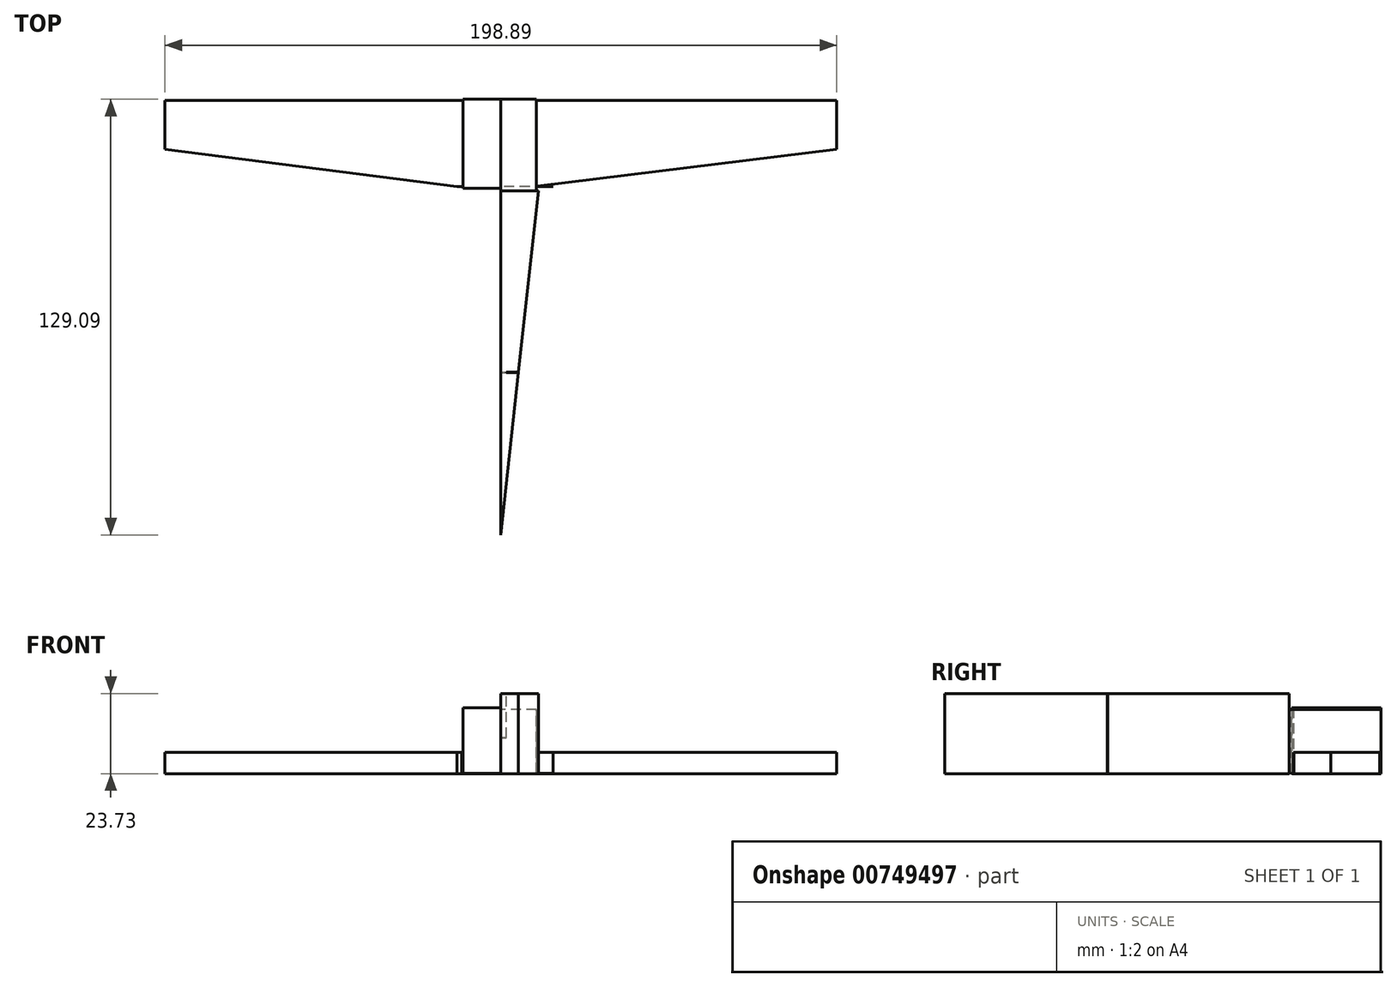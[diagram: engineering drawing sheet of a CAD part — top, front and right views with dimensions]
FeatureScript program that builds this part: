
annotation { "Feature Type Name" : "Feature", "Feature Type Description" : "" }
export const myFeature = defineFeature(function(context is Context, id is Id, definition is map)
    precondition{}
    {
        {
            var Q0;
            Q0=qCreatedBy(makeId("Top.planeOp"),FACE);
            var sketch = newSketch(context, id + "F0", { "sketchPlane" : qUnion([Q0])});
            skLineSegment(sketch, "E0.bottom", {"start": v(99.53, 14.5) * mm, "end": v(-99.36, 14.5) * mm});
            skLineSegment(sketch, "E0.top", {"start": v(99.53, -11.1) * mm, "end": v(-99.36, -11.1) * mm});
            skLineSegment(sketch, "E0.left", {"start": v(99.53, 14.5) * mm, "end": v(99.53, -11.1) * mm});
            skLineSegment(sketch, "E0.right", {"start": v(-99.36, 14.5) * mm, "end": v(-99.36, -11.1) * mm});
            skSolve(sketch);
        }
        {
            var Q0;
            Q0 = qSketchRegion(id + "F0", true);
            extrude(context, id + "F1", {"entities" : qUnion([Q0]), "depth" : 6.35 * mm, "offsetDistance" : 25.4 * mm});
        }
        {
            var Q0;
            Q0=qCreatedBy(makeId("Top.planeOp"),FACE);
            var sketch = newSketch(context, id + "F2", { "sketchPlane" : qUnion([Q0])});
            skLineSegment(sketch, "E1.bottom", {"start": v(-11.18, 14.82) * mm, "end": v(10.66, 14.82) * mm});
            skLineSegment(sketch, "E1.top", {"start": v(-11.18, -76.16) * mm, "end": v(10.66, -76.16) * mm});
            skLineSegment(sketch, "E1.left", {"start": v(-11.18, 14.82) * mm, "end": v(-11.18, -76.16) * mm});
            skLineSegment(sketch, "E1.right", {"start": v(10.66, 14.82) * mm, "end": v(10.66, -76.16) * mm});
            skSolve(sketch);
        }
        {
            var Q0;
            Q0 = qSketchRegion(id + "F2", true);
            extrude(context, id + "F3", {"entities" : qUnion([Q0]), "operationType" : NewBodyOperationType.ADD, "depth" : 25.4 * mm, "offsetDistance" : 25.4 * mm});
        }
        {
            var Q0;
            Q0=qCreatedBy(makeId("Right.planeOp"),FACE);
            var sketch = newSketch(context, id + "F4", { "sketchPlane" : qUnion([Q0])});
            skLineSegment(sketch, "E2", {"start": v(-11.26, 0) * mm, "end": v(-76.37, 12.55) * mm});
            skLineSegment(sketch, "E3", {"start": v(-76.37, 12.55) * mm, "end": v(-76.37, 0) * mm});
            skLineSegment(sketch, "E4", {"start": v(-76.37, 0) * mm, "end": v(-11.26, 0) * mm});
            skSolve(sketch);
        }
        {
            var Q0;
            Q0 = qSketchRegion(id + "F4", true);
            extrude(context, id + "F5", {"entities" : qUnion([Q0]), "operationType" : NewBodyOperationType.REMOVE, "oppositeDirection" : true, "depth" : 14.73 * mm, "offsetDistance" : 25.4 * mm});
        }
        {
            var Q0;
            Q0=qCreatedBy(makeId("Right.planeOp"),FACE);
            var sketch = newSketch(context, id + "F6", { "sketchPlane" : qUnion([Q0])});
            skLineSegment(sketch, "E5", {"start": v(-11.02, 0) * mm, "end": v(-75.8, 12.55) * mm});
            skLineSegment(sketch, "E6", {"start": v(-75.8, 12.55) * mm, "end": v(-75.8, 0) * mm});
            skLineSegment(sketch, "E7", {"start": v(-75.8, 0) * mm, "end": v(-11.02, 0) * mm});
            skSolve(sketch);
        }
        {
            var Q0;
            Q0 = qSketchRegion(id + "F6", true);
            extrude(context, id + "F7", {"entities" : qUnion([Q0]), "operationType" : NewBodyOperationType.REMOVE, "depth" : 19.56 * mm, "offsetDistance" : 25.4 * mm});
        }
        {
            var Q0;
            Q0=qCreatedBy(makeId("Right.planeOp"),FACE);
            var sketch = newSketch(context, id + "F8", { "sketchPlane" : qUnion([Q0])});
            skLineSegment(sketch, "E8", {"start": v(-74.42, 11.26) * mm, "end": v(-78.63, 14.66) * mm});
            skLineSegment(sketch, "E9", {"start": v(-78.63, 14.66) * mm, "end": v(-78.63, -1.38) * mm});
            skLineSegment(sketch, "E10", {"start": v(-78.63, -1.38) * mm, "end": v(-71.83, -1.38) * mm});
            skLineSegment(sketch, "E11", {"start": v(-71.83, -1.38) * mm, "end": v(-74.42, 9.96) * mm});
            skLineSegment(sketch, "E12", {"start": v(-74.42, 9.96) * mm, "end": v(-74.42, 11.26) * mm});
            skSolve(sketch);
        }
        {
            var Q0;
            Q0 = qSketchRegion(id + "F8", true);
            extrude(context, id + "F9", {"entities" : qUnion([Q0]), "operationType" : NewBodyOperationType.REMOVE, "depth" : 22.1 * mm, "offsetDistance" : 25.4 * mm});
        }
        {
            var Q0;
            Q0=qCreatedBy(makeId("Top.planeOp"),FACE);
            var sketch = newSketch(context, id + "F10", { "sketchPlane" : qUnion([Q0])});
            skLineSegment(sketch, "E13", {"start": v(-11.18, -11.1) * mm, "end": v(0, -76.2) * mm});
            skLineSegment(sketch, "E14", {"start": v(0, -76.2) * mm, "end": v(-11.01, -76.2) * mm});
            skLineSegment(sketch, "E15", {"start": v(-11.01, -76.2) * mm, "end": v(-11.18, -11.1) * mm});
            skSolve(sketch);
        }
        {
            var Q0;
            Q0 = qSketchRegion(id + "F10", true);
            extrude(context, id + "F11", {"entities" : qUnion([Q0]), "operationType" : NewBodyOperationType.REMOVE, "depth" : 46.48 * mm, "offsetDistance" : 25.4 * mm});
        }
        {
            var Q0;
            Q0=qCreatedBy(makeId("Top.planeOp"),FACE);
            var sketch = newSketch(context, id + "F12", { "sketchPlane" : qUnion([Q0])});
            skLineSegment(sketch, "E16", {"start": v(10.85, -11.26) * mm, "end": v(0, -76.2) * mm});
            skLineSegment(sketch, "E17", {"start": v(0, -76.2) * mm, "end": v(12.8, -76.2) * mm});
            skLineSegment(sketch, "E18", {"start": v(12.8, -76.2) * mm, "end": v(10.85, -11.26) * mm});
            skSolve(sketch);
        }
        {
            var Q0;
            Q0 = qSketchRegion(id + "F12", true);
            extrude(context, id + "F13", {"entities" : qUnion([Q0]), "operationType" : NewBodyOperationType.REMOVE, "depth" : 44.96 * mm, "offsetDistance" : 25.4 * mm});
        }
        {
            var Q0;
            Q0=qCreatedBy(makeId("Top.planeOp"),FACE);
            var sketch = newSketch(context, id + "F14", { "sketchPlane" : qUnion([Q0])});
            skLineSegment(sketch, "E19", {"start": v(-11.5, -10.93) * mm, "end": v(-5.02, -78.3) * mm});
            skLineSegment(sketch, "E20", {"start": v(-5.02, -78.3) * mm, "end": v(-21.87, -76.85) * mm});
            skLineSegment(sketch, "E21", {"start": v(-21.87, -76.85) * mm, "end": v(-11.5, -10.93) * mm});
            skSolve(sketch);
        }
        {
            var Q0;
            Q0 = qSketchRegion(id + "F14", true);
            extrude(context, id + "F15", {"entities" : qUnion([Q0]), "operationType" : NewBodyOperationType.REMOVE, "depth" : 55.63 * mm, "offsetDistance" : 25.4 * mm});
        }
        {
            var Q0;
            Q0=qCreatedBy(makeId("Top.planeOp"),FACE);
            var sketch = newSketch(context, id + "F16", { "sketchPlane" : qUnion([Q0])});
            skLineSegment(sketch, "E22", {"start": v(-11.34, -11.26) * mm, "end": v(-5.5, -77.01) * mm});
            skLineSegment(sketch, "E23", {"start": v(-5.5, -77.01) * mm, "end": v(-23.48, -75.56) * mm});
            skLineSegment(sketch, "E24", {"start": v(-23.48, -75.56) * mm, "end": v(-11.34, -11.26) * mm});
            skSolve(sketch);
        }
        {
            var Q0;
            Q0 = qSketchRegion(id + "F16", true);
            extrude(context, id + "F17", {"entities" : qUnion([Q0]), "operationType" : NewBodyOperationType.REMOVE, "depth" : 57.15 * mm, "offsetDistance" : 25.4 * mm});
        }
        {
            var Q0;
            Q0=qCreatedBy(makeId("Top.planeOp"),FACE);
            var sketch = newSketch(context, id + "F18", { "sketchPlane" : qUnion([Q0])});
            skLineSegment(sketch, "E25", {"start": v(10.85, -10.93) * mm, "end": v(99.77, 0) * mm});
            skLineSegment(sketch, "E26", {"start": v(99.77, 0) * mm, "end": v(99.77, -14) * mm});
            skLineSegment(sketch, "E27", {"start": v(99.77, -14) * mm, "end": v(10.85, -10.93) * mm});
            skSolve(sketch);
        }
        {
            var Q0;
            Q0 = qSketchRegion(id + "F18", true);
            extrude(context, id + "F19", {"entities" : qUnion([Q0]), "operationType" : NewBodyOperationType.REMOVE, "depth" : 63 * mm, "offsetDistance" : 25.4 * mm});
        }
        {
            var Q0;
            Q0=qCreatedBy(makeId("Top.planeOp"),FACE);
            var sketch = newSketch(context, id + "F20", { "sketchPlane" : qUnion([Q0])});
            skLineSegment(sketch, "E28", {"start": v(-11.66, -11.26) * mm, "end": v(-99.6, 0) * mm});
            skLineSegment(sketch, "E29", {"start": v(-99.6, 0) * mm, "end": v(-99.6, -13.2) * mm});
            skLineSegment(sketch, "E30", {"start": v(-99.6, -13.2) * mm, "end": v(-11.66, -11.26) * mm});
            skSolve(sketch);
        }
        {
            var Q0;
            Q0 = qSketchRegion(id + "F20", true);
            extrude(context, id + "F21", {"entities" : qUnion([Q0]), "operationType" : NewBodyOperationType.REMOVE, "depth" : 35.3 * mm, "offsetDistance" : 25.4 * mm});
        }
        {
            var Q0;
            Q0=qCreatedBy(makeId("Right.planeOp"),FACE);
            var sketch = newSketch(context, id + "F22", { "sketchPlane" : qUnion([Q0])});
            skLineSegment(sketch, "E31.bottom", {"start": v(-24.86, 25.5) * mm, "end": v(14.98, 25.5) * mm});
            skLineSegment(sketch, "E31.top", {"start": v(-24.86, 19.03) * mm, "end": v(14.98, 19.03) * mm});
            skLineSegment(sketch, "E31.left", {"start": v(-24.86, 25.5) * mm, "end": v(-24.86, 19.03) * mm});
            skLineSegment(sketch, "E31.right", {"start": v(14.98, 25.5) * mm, "end": v(14.98, 19.03) * mm});
            skSolve(sketch);
        }
        {
            var Q0;
            Q0 = qSketchRegion(id + "F22", true);
            extrude(context, id + "F23", {"entities" : qUnion([Q0]), "operationType" : NewBodyOperationType.REMOVE, "depth" : 25.9 * mm, "offsetDistance" : 25.4 * mm});
        }
        {
            var Q0;
            Q0=qCreatedBy(makeId("Right.planeOp"),FACE);
            var sketch = newSketch(context, id + "F24", { "sketchPlane" : qUnion([Q0])});
            skLineSegment(sketch, "E32.bottom", {"start": v(-24.54, 19.52) * mm, "end": v(14.5, 19.52) * mm});
            skLineSegment(sketch, "E32.top", {"start": v(-24.54, 25.5) * mm, "end": v(14.5, 25.5) * mm});
            skLineSegment(sketch, "E32.left", {"start": v(-24.54, 19.52) * mm, "end": v(-24.54, 25.5) * mm});
            skLineSegment(sketch, "E32.right", {"start": v(14.5, 19.52) * mm, "end": v(14.5, 25.5) * mm});
            skSolve(sketch);
        }
        {
            var Q0;
            Q0 = qSketchRegion(id + "F24", true);
            extrude(context, id + "F25", {"entities" : qUnion([Q0]), "operationType" : NewBodyOperationType.REMOVE, "oppositeDirection" : true, "depth" : 22.6 * mm, "offsetDistance" : 25.4 * mm});
        }
        {
            var Q0;
            Q0=qCreatedBy(makeId("Right.planeOp"),FACE);
            var sketch = newSketch(context, id + "F26", { "sketchPlane" : qUnion([Q0])});
            skLineSegment(sketch, "E33.bottom", {"start": v(-17.41, 19.68) * mm, "end": v(31.83, 19.68) * mm});
            skLineSegment(sketch, "E33.top", {"start": v(-17.41, 26.97) * mm, "end": v(31.83, 26.97) * mm});
            skLineSegment(sketch, "E33.left", {"start": v(-17.41, 19.68) * mm, "end": v(-17.41, 26.97) * mm});
            skLineSegment(sketch, "E33.right", {"start": v(31.83, 19.68) * mm, "end": v(31.83, 26.97) * mm});
            skSolve(sketch);
        }
        {
            var Q0;
            Q0 = qSketchRegion(id + "F26", true);
            extrude(context, id + "F27", {"entities" : qUnion([Q0]), "operationType" : NewBodyOperationType.REMOVE, "oppositeDirection" : true, "depth" : 24.38 * mm, "offsetDistance" : 25.4 * mm});
        }
        {
            var Q0;
            Q0=qCreatedBy(makeId("Right.planeOp"),FACE);
            var sketch = newSketch(context, id + "F28", { "sketchPlane" : qUnion([Q0])});
            skLineSegment(sketch, "E34.bottom", {"start": v(-24.21, 19.52) * mm, "end": v(27.78, 19.52) * mm});
            skLineSegment(sketch, "E34.top", {"start": v(-24.21, 26.16) * mm, "end": v(27.78, 26.16) * mm});
            skLineSegment(sketch, "E34.left", {"start": v(-24.21, 19.52) * mm, "end": v(-24.21, 26.16) * mm});
            skLineSegment(sketch, "E34.right", {"start": v(27.78, 19.52) * mm, "end": v(27.78, 26.16) * mm});
            skSolve(sketch);
        }
        {
            var Q0;
            Q0 = qSketchRegion(id + "F28", true);
            extrude(context, id + "F29", {"entities" : qUnion([Q0]), "operationType" : NewBodyOperationType.REMOVE, "oppositeDirection" : true, "depth" : 18.29 * mm, "offsetDistance" : 25.4 * mm});
        }
        {
            var Q0;
            Q0=qCreatedBy(makeId("Right.planeOp"),FACE);
            var sketch = newSketch(context, id + "F30", { "sketchPlane" : qUnion([Q0])});
            skLineSegment(sketch, "E35.bottom", {"start": v(-76.2, 28.42) * mm, "end": v(-66, 28.42) * mm});
            skLineSegment(sketch, "E35.top", {"start": v(-76.2, 5.59) * mm, "end": v(-66, 5.59) * mm});
            skLineSegment(sketch, "E35.left", {"start": v(-76.2, 28.42) * mm, "end": v(-76.2, 5.59) * mm});
            skLineSegment(sketch, "E35.right", {"start": v(-66, 28.42) * mm, "end": v(-66, 5.59) * mm});
            skSolve(sketch);
        }
        {
            var Q0;
            Q0 = qSketchRegion(id + "F30", true);
            extrude(context, id + "F31", {"entities" : qUnion([Q0]), "operationType" : NewBodyOperationType.REMOVE, "oppositeDirection" : true, "depth" : 33.78 * mm, "offsetDistance" : 25.4 * mm});
        }
        {
            var Q0;
            Q0=qCreatedBy(makeId("Right.planeOp"),FACE);
            var sketch = newSketch(context, id + "F32", { "sketchPlane" : qUnion([Q0])});
            skLineSegment(sketch, "E36.bottom", {"start": v(-76.37, 28.59) * mm, "end": v(-66.16, 28.59) * mm});
            skLineSegment(sketch, "E36.top", {"start": v(-76.37, 7.86) * mm, "end": v(-66.16, 7.86) * mm});
            skLineSegment(sketch, "E36.left", {"start": v(-76.37, 28.59) * mm, "end": v(-76.37, 7.86) * mm});
            skLineSegment(sketch, "E36.right", {"start": v(-66.16, 28.59) * mm, "end": v(-66.16, 7.86) * mm});
            skSolve(sketch);
        }
        {
            var Q0;
            Q0 = qSketchRegion(id + "F32", true);
            extrude(context, id + "F33", {"entities" : qUnion([Q0]), "operationType" : NewBodyOperationType.REMOVE, "depth" : 41.4 * mm, "offsetDistance" : 25.4 * mm});
        }
        {
            var Q0;
            Q0=qCreatedBy(makeId("Right.planeOp"),FACE);
            var sketch = newSketch(context, id + "F34", { "sketchPlane" : qUnion([Q0])});
            skLineSegment(sketch, "E37.bottom", {"start": v(-66.16, 25.67) * mm, "end": v(-114.27, 25.67) * mm});
            skLineSegment(sketch, "E37.top", {"start": v(-66.16, 0) * mm, "end": v(-114.27, 0) * mm});
            skLineSegment(sketch, "E37.left", {"start": v(-66.16, 25.67) * mm, "end": v(-66.16, 0) * mm});
            skLineSegment(sketch, "E37.right", {"start": v(-114.27, 25.67) * mm, "end": v(-114.27, 0) * mm});
            skSolve(sketch);
        }
        {
            var Q0;
            Q0 = qSketchRegion(id + "F34", true);
            extrude(context, id + "F35", {"entities" : qUnion([Q0]), "operationType" : NewBodyOperationType.ADD, "depth" : 25.4 * mm, "offsetDistance" : 25.4 * mm});
        }
        {
            var Q0;
            Q0=qCreatedBy(makeId("Right.planeOp"),FACE);
            var sketch = newSketch(context, id + "F36", { "sketchPlane" : qUnion([Q0])});
            skLineSegment(sketch, "E38.bottom", {"start": v(-66.08, 26.8) * mm, "end": v(-12.31, 26.8) * mm});
            skLineSegment(sketch, "E38.top", {"start": v(-66.08, 0) * mm, "end": v(-12.31, 0) * mm});
            skLineSegment(sketch, "E38.left", {"start": v(-66.08, 26.8) * mm, "end": v(-66.08, 0) * mm});
            skLineSegment(sketch, "E38.right", {"start": v(-12.31, 26.8) * mm, "end": v(-12.31, 0) * mm});
            skSolve(sketch);
        }
        {
            var Q0;
            Q0 = qSketchRegion(id + "F36", true);
            extrude(context, id + "F37", {"entities" : qUnion([Q0]), "operationType" : NewBodyOperationType.ADD, "depth" : 25.4 * mm, "offsetDistance" : 25.4 * mm});
        }
        {
            var Q0;
            Q0=qCreatedBy(makeId("Right.planeOp"),FACE);
            var sketch = newSketch(context, id + "F38", { "sketchPlane" : qUnion([Q0])});
            skLineSegment(sketch, "E39.bottom", {"start": v(-116.45, 26.8) * mm, "end": v(-12.64, 26.8) * mm});
            skLineSegment(sketch, "E39.top", {"start": v(-116.45, 0) * mm, "end": v(-12.64, 0) * mm});
            skLineSegment(sketch, "E39.left", {"start": v(-116.45, 26.8) * mm, "end": v(-116.45, 0) * mm});
            skLineSegment(sketch, "E39.right", {"start": v(-12.64, 26.8) * mm, "end": v(-12.64, 0) * mm});
            skSolve(sketch);
        }
        {
            var Q0;
            Q0 = qSketchRegion(id + "F38", true);
            extrude(context, id + "F39", {"entities" : qUnion([Q0]), "oppositeDirection" : true, "depth" : 12.7 * mm, "offsetDistance" : 25.4 * mm});
        }
        {
            var Q0;
            Q0=qCreatedBy(makeId("Top.planeOp"),FACE);
            var sketch = newSketch(context, id + "F40", { "sketchPlane" : qUnion([Q0])});
            skLineSegment(sketch, "E40", {"start": v(-11.1, -11.96) * mm, "end": v(0, -114.28) * mm});
            skLineSegment(sketch, "E41", {"start": v(0, -114.28) * mm, "end": v(0, -120.64) * mm});
            skLineSegment(sketch, "E42", {"start": v(0, -120.64) * mm, "end": v(-33.65, -114.28) * mm});
            skLineSegment(sketch, "E43", {"start": v(-33.65, -114.28) * mm, "end": v(-11.1, -11.96) * mm});
            skSolve(sketch);
        }
        {
            var Q0;
            Q0 = qSketchRegion(id + "F40", true);
            extrude(context, id + "F41", {"entities" : qUnion([Q0]), "operationType" : NewBodyOperationType.REMOVE, "depth" : 52.07 * mm, "offsetDistance" : 25.4 * mm});
        }
        {
            var Q0;
            Q0=qCreatedBy(makeId("Top.planeOp"),FACE);
            var sketch = newSketch(context, id + "F42", { "sketchPlane" : qUnion([Q0])});
            skLineSegment(sketch, "E44", {"start": v(11.26, -11.96) * mm, "end": v(0, -114.28) * mm});
            skLineSegment(sketch, "E45", {"start": v(0, -114.28) * mm, "end": v(0, -117.36) * mm});
            skLineSegment(sketch, "E46", {"start": v(0, -117.36) * mm, "end": v(38.94, -117.36) * mm});
            skLineSegment(sketch, "E47", {"start": v(38.94, -117.36) * mm, "end": v(36.68, -11.55) * mm});
            skLineSegment(sketch, "E48", {"start": v(36.68, -11.55) * mm, "end": v(11.26, -11.96) * mm});
            skSolve(sketch);
        }
        {
            var Q0;
            Q0 = qSketchRegion(id + "F42", true);
            extrude(context, id + "F43", {"entities" : qUnion([Q0]), "operationType" : NewBodyOperationType.REMOVE, "depth" : 85.1 * mm, "offsetDistance" : 25.4 * mm});
        }
        {
            var Q0;
            Q0=qCreatedBy(makeId("Top.planeOp"),FACE);
            var sketch = newSketch(context, id + "F44", { "sketchPlane" : qUnion([Q0])});
            skLineSegment(sketch, "E49", {"start": v(-11.1, -23.45) * mm, "end": v(-11.1, -11.35) * mm});
            skLineSegment(sketch, "E50", {"start": v(-11.1, -11.35) * mm, "end": v(-35.7, -14.63) * mm});
            skLineSegment(sketch, "E51", {"start": v(-35.7, -14.63) * mm, "end": v(-11.1, -23.45) * mm});
            skSolve(sketch);
        }
        {
            var Q0;
            Q0 = qSketchRegion(id + "F44", true);
            extrude(context, id + "F45", {"entities" : qUnion([Q0]), "operationType" : NewBodyOperationType.REMOVE, "depth" : 60.45 * mm, "offsetDistance" : 25.4 * mm});
        }
        {
            var Q0;
            Q0=qCreatedBy(makeId("Right.planeOp"),FACE);
            var sketch = newSketch(context, id + "F46", { "sketchPlane" : qUnion([Q0])});
            skLineSegment(sketch, "E52", {"start": v(-9.34, 23.73) * mm, "end": v(-118.5, 23.73) * mm});
            skLineSegment(sketch, "E53", {"start": v(-118.5, 23.73) * mm, "end": v(-118.5, 31.18) * mm});
            skLineSegment(sketch, "E54", {"start": v(-118.5, 31.18) * mm, "end": v(-6.75, 31.18) * mm});
            skLineSegment(sketch, "E55", {"start": v(-6.75, 31.18) * mm, "end": v(-9.34, 23.73) * mm});
            skSolve(sketch);
        }
        {
            var Q0;
            Q0 = qSketchRegion(id + "F46", true);
            extrude(context, id + "F47", {"entities" : qUnion([Q0]), "operationType" : NewBodyOperationType.REMOVE, "depth" : 21.08 * mm, "offsetDistance" : 25.4 * mm});
        }
        {
            var Q0;
            Q0=qCreatedBy(makeId("Right.planeOp"),FACE);
            var sketch = newSketch(context, id + "F48", { "sketchPlane" : qUnion([Q0])});
            skLineSegment(sketch, "E56", {"start": v(-11.51, 27.13) * mm, "end": v(-11.51, -14.66) * mm});
            skLineSegment(sketch, "E57", {"start": v(-11.51, -14.66) * mm, "end": v(-141.25, -14.66) * mm});
            skLineSegment(sketch, "E58", {"start": v(-141.25, -14.66) * mm, "end": v(-138.5, 40.25) * mm});
            skLineSegment(sketch, "E59", {"start": v(-138.5, 40.25) * mm, "end": v(-11.51, 27.13) * mm});
            skSolve(sketch);
        }
        {
            var Q0;
            Q0 = qSketchRegion(id + "F48", true);
            extrude(context, id + "F49", {"entities" : qUnion([Q0]), "operationType" : NewBodyOperationType.REMOVE, "oppositeDirection" : true, "depth" : 41.66 * mm, "offsetDistance" : 25.4 * mm});
        }
    });
